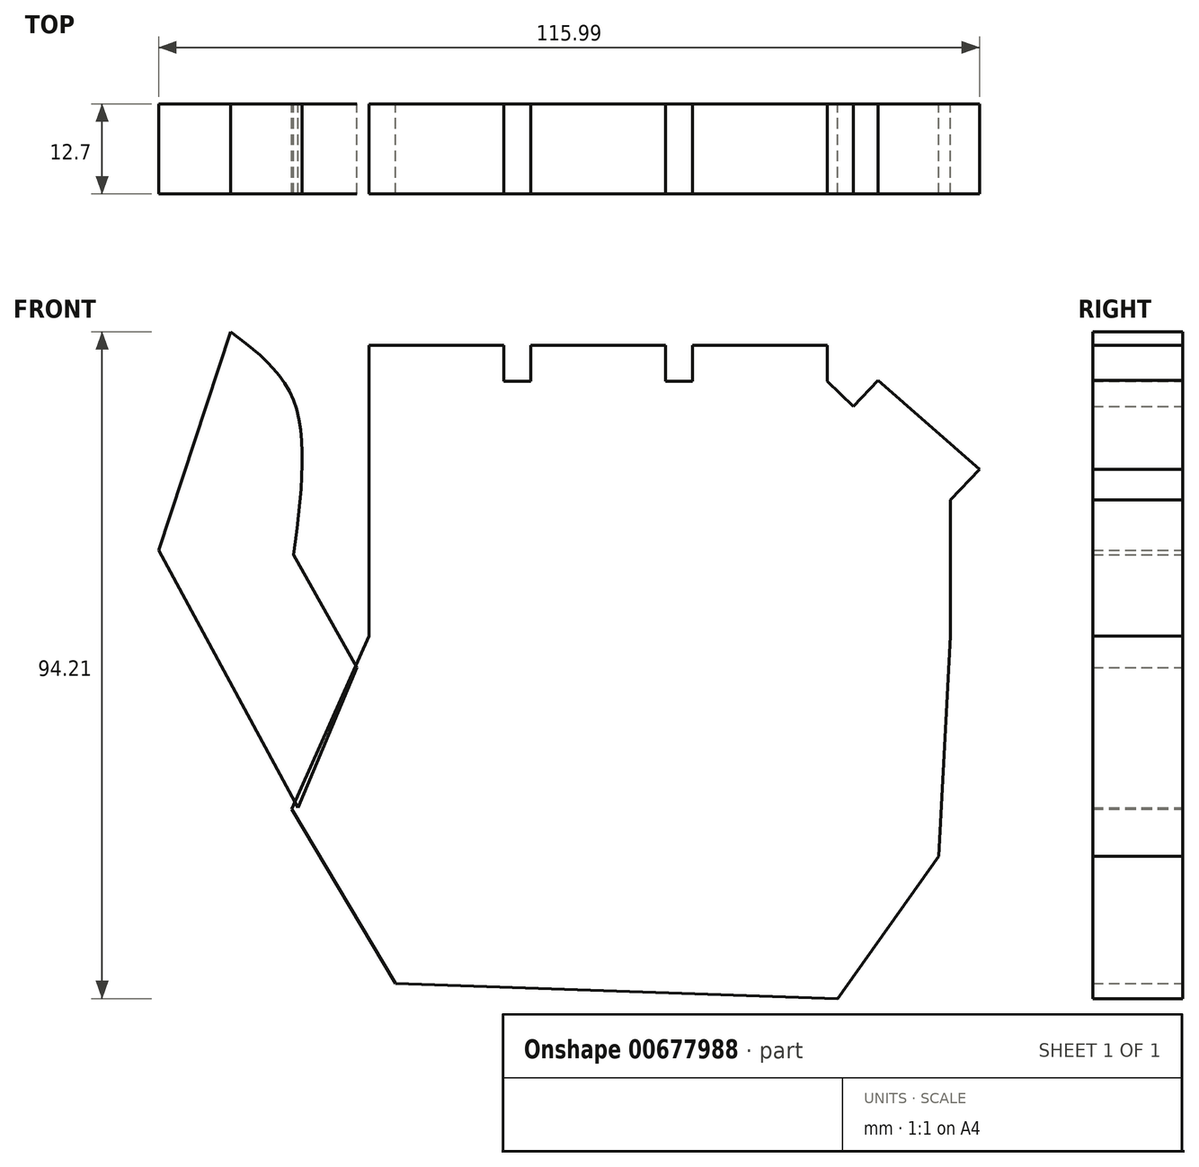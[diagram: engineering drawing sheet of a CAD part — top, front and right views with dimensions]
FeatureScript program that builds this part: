
annotation { "Feature Type Name" : "Feature", "Feature Type Description" : "" }
export const myFeature = defineFeature(function(context is Context, id is Id, definition is map)
    precondition{}
    {
        {
            var Q0;
            Q0=qCreatedBy(makeId("Front.planeOp"),FACE);
            var sketch = newSketch(context, id + "F0", { "sketchPlane" : qUnion([Q0])});
            skLineSegment(sketch, "E0.bottom", {"start": v(-39.98, 23.71) * mm, "end": v(42.2, 23.71) * mm});
            skLineSegment(sketch, "E0.top", {"start": v(-39.98, 4.47) * mm, "end": v(42.2, 4.47) * mm});
            skLineSegment(sketch, "E0.left", {"start": v(-39.98, 23.71) * mm, "end": v(-39.98, 4.47) * mm});
            skLineSegment(sketch, "E0.right", {"start": v(42.2, 23.71) * mm, "end": v(42.2, 4.47) * mm});
            skLineSegment(sketch, "E1", {"start": v(42.2, 23.71) * mm, "end": v(24.8, 40.43) * mm});
            skLineSegment(sketch, "E2", {"start": v(-39.98, 23.71) * mm, "end": v(-39.98, 40.43) * mm});
            skLineSegment(sketch, "E3", {"start": v(-39.98, 40.43) * mm, "end": v(24.8, 40.43) * mm});
            skLineSegment(sketch, "E4", {"start": v(-39.98, 4.47) * mm, "end": v(40.55, -26.62) * mm});
            skLineSegment(sketch, "E5", {"start": v(40.55, -26.62) * mm, "end": v(42.2, 4.47) * mm});
            skLineSegment(sketch, "E6", {"start": v(-39.98, 40.43) * mm, "end": v(-39.98, 45.51) * mm});
            skLineSegment(sketch, "E7", {"start": v(-20.93, 40.43) * mm, "end": v(-20.93, 45.51) * mm});
            skLineSegment(sketch, "E8", {"start": v(1.93, 40.43) * mm, "end": v(1.93, 45.51) * mm});
            skLineSegment(sketch, "E9", {"start": v(-17.12, 40.43) * mm, "end": v(-17.12, 45.51) * mm});
            skLineSegment(sketch, "E10", {"start": v(5.74, 40.43) * mm, "end": v(5.74, 45.51) * mm});
            skLineSegment(sketch, "E11", {"start": v(24.8, 40.43) * mm, "end": v(24.8, 45.51) * mm});
            skLineSegment(sketch, "E12", {"start": v(42.2, 23.71) * mm, "end": v(46.3, 28) * mm});
            skLineSegment(sketch, "E13", {"start": v(-39.98, 45.51) * mm, "end": v(-20.93, 45.51) * mm});
            skLineSegment(sketch, "E14", {"start": v(-17.12, 45.51) * mm, "end": v(1.93, 45.51) * mm});
            skLineSegment(sketch, "E15", {"start": v(5.74, 45.51) * mm, "end": v(24.8, 45.51) * mm});
            skLineSegment(sketch, "E16", {"start": v(28.47, 36.9) * mm, "end": v(31.99, 40.56) * mm});
            skLineSegment(sketch, "E17", {"start": v(31.99, 40.56) * mm, "end": v(46.3, 28) * mm});
            skPoint(sketch, "E18", {"position": v(44.25, 25.86) * mm});
            skPoint(sketch, "E19", {"position": v(30.23, 38.73) * mm});
            skPoint(sketch, "E20", {"position": v(39.15, 34.28) * mm});
            skPoint(sketch, "E21", {"position": v(12.3, 11.02) * mm});
            skLineSegment(sketch, "E22", {"start": v(40.55, -26.62) * mm, "end": v(26.28, -46.76) * mm});
            skLineSegment(sketch, "E23", {"start": v(-36.18, -44.63) * mm, "end": v(-50.9, -20) * mm});
            skLineSegment(sketch, "E24", {"start": v(26.28, -46.76) * mm, "end": v(-36.18, -44.63) * mm});
            skLineSegment(sketch, "E25", {"start": v(-39.98, 4.47) * mm, "end": v(-50.9, -20) * mm});
            skSolve(sketch);
        }
        {
            var Q0;
            Q0 = qSketchRegion(id + "F0", true);
            extrude(context, id + "F1", {"entities" : qUnion([Q0]), "endBound" : BoundingType.SYMMETRIC, "depth" : 12.7 * mm, "offsetDistance" : 25.4 * mm});
        }
        {
            var Q0;
            Q0=qCreatedBy(makeId("Front.planeOp"),FACE);
            var sketch = newSketch(context, id + "F2", { "sketchPlane" : qUnion([Q0])});
            skLineSegment(sketch, "E26", {"start": v(-50, -19.82) * mm, "end": v(-69.68, 16.57) * mm});
            skLineSegment(sketch, "E27", {"start": v(-41.68, 0) * mm, "end": v(-50.63, 15.93) * mm});
            skLineSegment(sketch, "E28", {"start": v(-50, -19.82) * mm, "end": v(-41.68, 0) * mm});
            skFitSpline(sketch, "E29", {"points": [v(-50.63, 15.93) * mm, v(-50.63, 37.75) * mm, v(-59.5, 47.45) * mm], "startDerivative": vector(5.72, 43.42) * mm, "endDerivative": vector(-24.74, 18.56) * mm});
            skLineSegment(sketch, "E30", {"start": v(-59.5, 47.45) * mm, "end": v(-69.68, 16.57) * mm});
            skSolve(sketch);
        }
        {
            var Q0;
            Q0 = qSketchRegion(id + "F2", true);
            extrude(context, id + "F3", {"entities" : qUnion([Q0]), "endBound" : BoundingType.SYMMETRIC, "depth" : 12.7 * mm, "offsetDistance" : 25.4 * mm});
        }
    });
